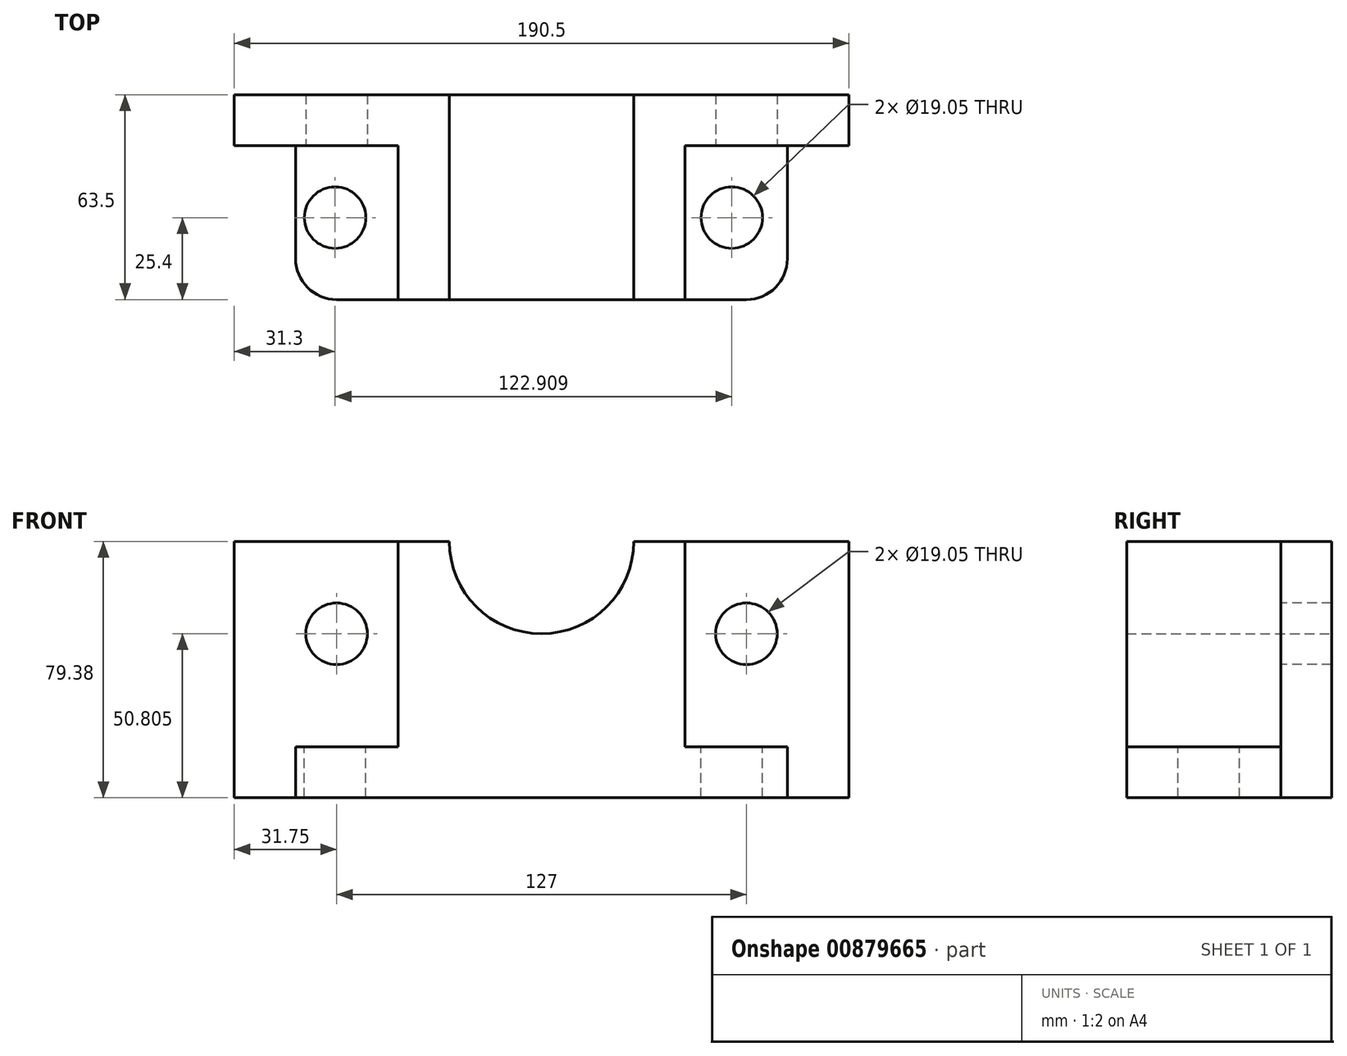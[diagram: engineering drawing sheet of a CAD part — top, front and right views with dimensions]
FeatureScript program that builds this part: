
annotation { "Feature Type Name" : "Feature", "Feature Type Description" : "" }
export const myFeature = defineFeature(function(context is Context, id is Id, definition is map)
    precondition{}
    {
        {
            var Q0;
            Q0=qCreatedBy(makeId("Front.planeOp"),FACE);
            var sketch = newSketch(context, id + "F0", { "sketchPlane" : qUnion([Q0])});
            skLineSegment(sketch, "E0.bottom", {"start": v(-95.25, 0) * mm, "end": v(-28.57, 0) * mm});
            skLineSegment(sketch, "E0.top", {"start": v(-95.25, -79.38) * mm, "end": v(95.25, -79.38) * mm});
            skLineSegment(sketch, "E0.left", {"start": v(-95.25, 0) * mm, "end": v(-95.25, -79.38) * mm});
            skLineSegment(sketch, "E0.right", {"start": v(95.25, 0) * mm, "end": v(95.25, -79.38) * mm});
            skArc(sketch, "E1", {"start": v(-28.58, 0) * mm, "mid": v(0, -28.58) * mm, "end": v(28.58, 0) * mm});
            skLineSegment(sketch, "E2.trimOffspring", {"start": v(28.58, 0) * mm, "end": v(95.25, 0) * mm});
            skSolve(sketch);
        }
        {
            var Q0;
            Q0 = qSketchRegion(id + "F0", true);
            extrude(context, id + "F1", {"entities" : qUnion([Q0]), "depth" : 15.75 * mm, "offsetDistance" : 25.4 * mm});
        }
        {
            var Q0;
            Q0=makeQuery(id+"F1.opExtrude","CAP_FACE",FACE,{"disambiguationData":[OSD([sQuery(id+"F0.wireOp",EDGE,"E0.bottom"),sQuery(id+"F0.wireOp",EDGE,"E0.top"),sQuery(id+"F0.wireOp",EDGE,"E0.left"),sQuery(id+"F0.wireOp",EDGE,"E0.right"),sQuery(id+"F0.wireOp",EDGE,"E1"),sQuery(id+"F0.wireOp",EDGE,"E2.trimOffspring")])],"isStart":false});
            var sketch = newSketch(context, id + "F2", { "sketchPlane" : qUnion([Q0])});
            skLineSegment(sketch, "E3", {"start": v(0, 0) * mm, "end": v(0, -98.16) * mm, "construction": true});
            skLineSegment(sketch, "E4", {"start": v(-44.45, 0) * mm, "end": v(-44.45, -79.38) * mm});
            skLineSegment(sketch, "E5.MirrorCS", {"start": v(44.45, 0) * mm, "end": v(44.45, -79.38) * mm});
            skSolve(sketch);
        }
        {
            var Q0;
            Q0 = qSketchRegion(id + "F2", true);
            var Q1;
            {var subQ2=sQuery(id+"F2.wireOp",EDGE,"E4");Q1=makeQuery(id+"F2.imprint","IMPRINT",FACE,{"disambiguationData":[TD([[makeQuery(id+"F2.imprint","IMPRINT",EDGE,{"derivedFrom":subQ2}),1.0]])]});}
            extrude(context, id + "F3", {"entities" : qUnion([Q0, Q1]), "operationType" : NewBodyOperationType.ADD, "depth" : 47.75 * mm, "offsetDistance" : 25.4 * mm});
        }
        {
            var Q0;
            Q0=makeQuery(id+"F3.opExtrude","CAP_FACE",FACE,{"disambiguationData":[OSD([sQuery(id+"F0.wireOp",EDGE,"E0.bottom"),sQuery(id+"F0.wireOp",EDGE,"E0.top"),sQuery(id+"F0.wireOp",EDGE,"E1"),sQuery(id+"F0.wireOp",EDGE,"E2.trimOffspring"),sQuery(id+"F2.wireOp",EDGE,"E4"),sQuery(id+"F2.wireOp",EDGE,"E5.MirrorCS")])],"isStart":false});
            var sketch = newSketch(context, id + "F4", { "sketchPlane" : qUnion([Q0])});
            skLineSegment(sketch, "E6.bottom", {"start": v(-76.2, -79.38) * mm, "end": v(76.2, -79.38) * mm});
            skLineSegment(sketch, "E6.top", {"start": v(-76.2, -63.63) * mm, "end": v(76.2, -63.63) * mm});
            skLineSegment(sketch, "E6.left", {"start": v(-76.2, -79.38) * mm, "end": v(-76.2, -63.63) * mm});
            skLineSegment(sketch, "E6.right", {"start": v(76.2, -79.38) * mm, "end": v(76.2, -63.63) * mm});
            skSolve(sketch);
        }
        {
            var Q0;
            Q0 = qSketchRegion(id + "F4", true);
            var Q1;
            {var subQ0=sQuery(id+"F0.wireOp",EDGE,"E2.trimOffspring");var subQ1=sQuery(id+"F0.wireOp",EDGE,"E0.top");var subQ2=sQuery(id+"F0.wireOp",EDGE,"E0.right");Q1=makeQuery(id+"F3.boolean.opBoolean","SPLIT",FACE,{"disambiguationData":[TD([makeQuery(id+"F1.opExtrude","SWEPT_FACE",FACE,{"disambiguationData":[OSD([subQ2])]})])],"derivedFrom":makeQuery(id+"F1.opExtrude","CAP_FACE",FACE,{"disambiguationData":[OSD([sQuery(id+"F0.wireOp",EDGE,"E0.bottom"),subQ1,sQuery(id+"F0.wireOp",EDGE,"E0.left"),subQ2,sQuery(id+"F0.wireOp",EDGE,"E1"),subQ0])],"isStart":false})});}
            extrude(context, id + "F5", {"entities" : qUnion([Q0]), "operationType" : NewBodyOperationType.ADD, "endBound" : BoundingType.UP_TO_SURFACE, "oppositeDirection" : true, "depth" : 25.4 * mm, "endBoundEntityFace" : qUnion([Q1]), "offsetDistance" : 25.4 * mm});
        }
        {
            var Q0;
            {var subQ1=sQuery(id+"F4.wireOp",EDGE,"E6.top");var subQ2=sQuery(id+"F2.wireOp",EDGE,"E5.MirrorCS");Q0=makeQuery(id+"F5.boolean.opBoolean","SPLIT",FACE,{"disambiguationData":[TD([makeQuery(id+"F3.opExtrude","SWEPT_FACE",FACE,{"disambiguationData":[OSD([subQ2])]})])],"derivedFrom":makeQuery(id+"F5.opExtrude","SWEPT_FACE",FACE,{"disambiguationData":[OSD([subQ1])]})});}
            var sketch = newSketch(context, id + "F6", { "sketchPlane" : qUnion([Q0])});
            skCircle(sketch, "E7", {"center": v(58.96, -38.1) * mm, "radius": 9.52 * mm});
            skSolve(sketch);
        }
        {
            var Q0;
            Q0=makeQuery(id+"F6.imprint","IMPRINT",FACE,{"disambiguationData":[TD([[makeQuery(id+"F6.imprint","IMPRINT",EDGE,{"derivedFrom":sQuery(id+"F6.wireOp",EDGE,"E7")}),1.0]])]});
            var Q1;
            Q1=sQuery(id+"F6.wireOp",EDGE,"E7");
            extrude(context, id + "F7", {"entities" : qUnion([Q0]), "operationType" : NewBodyOperationType.REMOVE, "surfaceEntities" : qUnion([Q1]), "endBound" : BoundingType.THROUGH_ALL, "oppositeDirection" : true, "depth" : 25.4 * mm, "offsetDistance" : 25.4 * mm});
        }
        {
            var Q0;
            Q0=makeQuery(id+"F5.opExtrude","CAP_EDGE",EDGE,{"disambiguationData":[OSD([sQuery(id+"F4.wireOp",EDGE,"E6.right")])],"isStart":true});
            var Q1;
            Q1=makeQuery(id+"F5.opExtrude","CAP_EDGE",EDGE,{"disambiguationData":[OSD([sQuery(id+"F4.wireOp",EDGE,"E6.left")])],"isStart":true});
            fillet(context, id + "F8", {"entities" : qUnion([Q0, Q1]), "radius" : 12.7 * mm, "tangentPropagation" : true, "allowEdgeOverflow" : false});
        }
        {
            var Q0;
            {var subQ0=sQuery(id+"F2.wireOp",EDGE,"E4");var subQ6=sQuery(id+"F4.wireOp",EDGE,"E6.top");Q0=makeQuery(id+"F5.boolean.opBoolean","SPLIT",FACE,{"disambiguationData":[TD([makeQuery(id+"F3.opExtrude","SWEPT_FACE",FACE,{"disambiguationData":[OSD([subQ0])]})])],"derivedFrom":makeQuery(id+"F5.opExtrude","SWEPT_FACE",FACE,{"disambiguationData":[OSD([subQ6])]})});}
            var sketch = newSketch(context, id + "F9", { "sketchPlane" : qUnion([Q0])});
            skCircle(sketch, "E8", {"center": v(-63.95, -38.1) * mm, "radius": 9.53 * mm});
            skSolve(sketch);
        }
        {
            var Q0;
            Q0 = qSketchRegion(id + "F9", true);
            extrude(context, id + "F10", {"entities" : qUnion([Q0]), "operationType" : NewBodyOperationType.REMOVE, "endBound" : BoundingType.THROUGH_ALL, "oppositeDirection" : true, "depth" : 25.4 * mm, "offsetDistance" : 25.4 * mm});
        }
        {
            var Q0;
            {var subQ0=sQuery(id+"F0.wireOp",EDGE,"E0.left");var subQ1=sQuery(id+"F0.wireOp",EDGE,"E0.top");var subQ2=sQuery(id+"F0.wireOp",EDGE,"E0.bottom");Q0=makeQuery(id+"F3.boolean.opBoolean","SPLIT",FACE,{"disambiguationData":[TD([makeQuery(id+"F1.opExtrude","SWEPT_FACE",FACE,{"disambiguationData":[OSD([subQ2])]})])],"derivedFrom":makeQuery(id+"F1.opExtrude","CAP_FACE",FACE,{"disambiguationData":[OSD([subQ2,subQ1,subQ0,sQuery(id+"F0.wireOp",EDGE,"E0.right"),sQuery(id+"F0.wireOp",EDGE,"E1"),sQuery(id+"F0.wireOp",EDGE,"E2.trimOffspring")])],"isStart":false})});}
            var sketch = newSketch(context, id + "F11", { "sketchPlane" : qUnion([Q0])});
            skCircle(sketch, "E9", {"center": v(-63.5, -28.58) * mm, "radius": 9.53 * mm});
            skCircle(sketch, "E10.MirrorC", {"center": v(63.5, -28.58) * mm, "radius": 9.53 * mm});
            skSolve(sketch);
        }
        {
            var Q0;
            Q0 = qSketchRegion(id + "F11", true);
            extrude(context, id + "F12", {"entities" : qUnion([Q0]), "operationType" : NewBodyOperationType.REMOVE, "endBound" : BoundingType.THROUGH_ALL, "oppositeDirection" : true, "depth" : 25.4 * mm, "offsetDistance" : 25.4 * mm});
        }
        {
            var Q0;
            Q0 = qSketchRegion(id + "F11", true);
            extrude(context, id + "F13", {"entities" : qUnion([Q0]), "operationType" : NewBodyOperationType.REMOVE, "oppositeDirection" : true, "depth" : 25.4 * mm, "offsetDistance" : 25.4 * mm});
        }
    });
